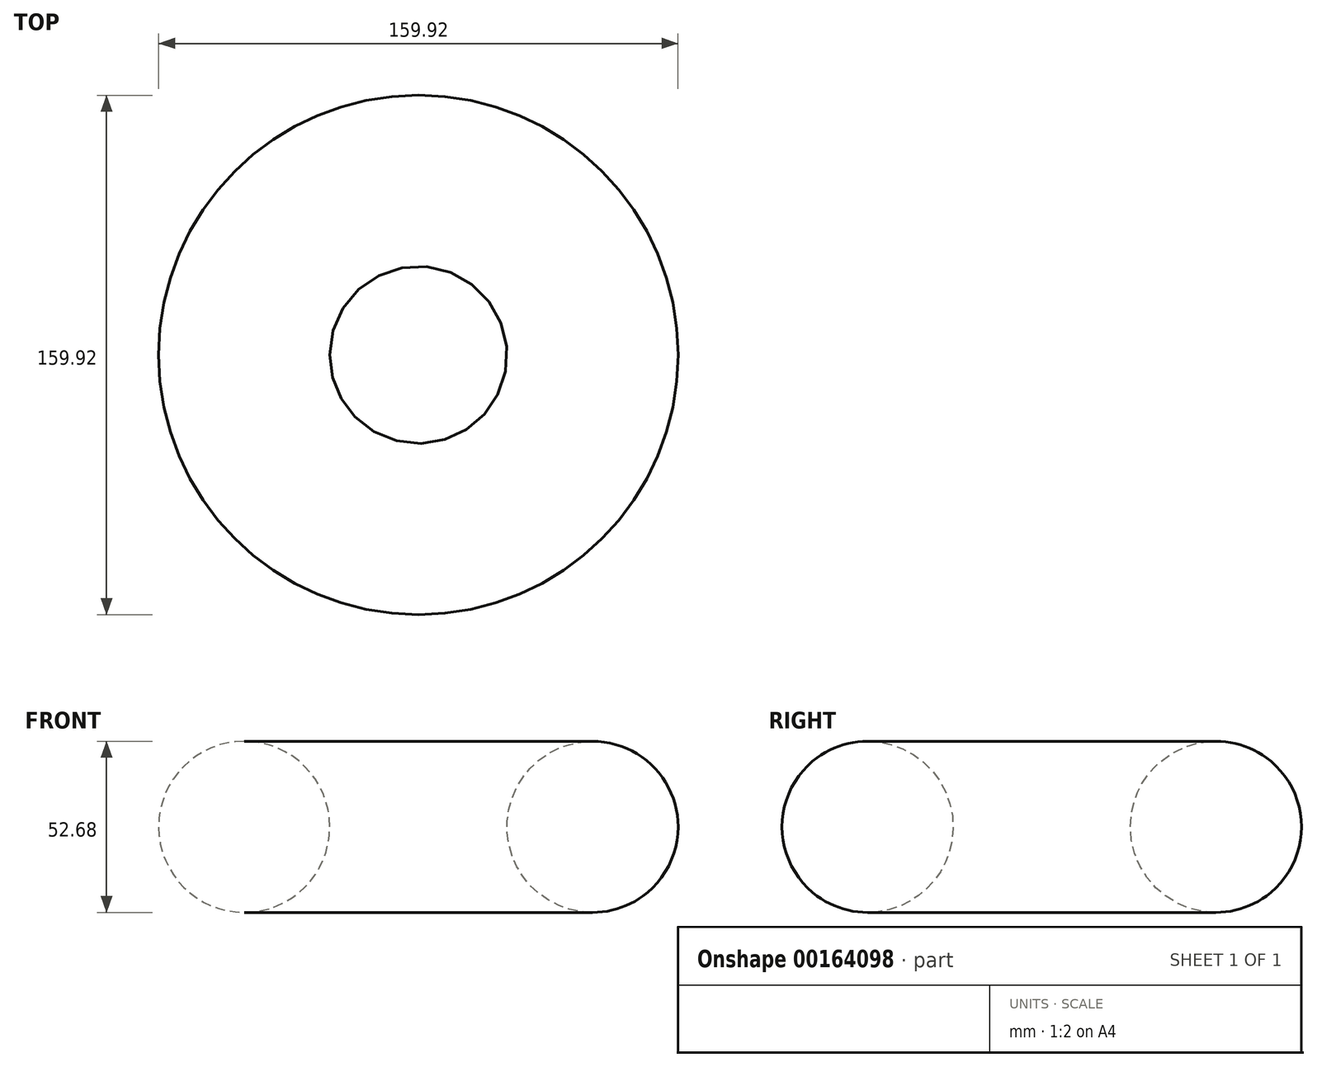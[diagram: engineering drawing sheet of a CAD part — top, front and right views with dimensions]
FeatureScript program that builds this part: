
annotation { "Feature Type Name" : "Feature", "Feature Type Description" : "" }
export const myFeature = defineFeature(function(context is Context, id is Id, definition is map)
    precondition{}
    {
        {
            var Q0;
            Q0=qCreatedBy(makeId("Front.planeOp"),FACE);
            var sketch = newSketch(context, id + "F0", { "sketchPlane" : qUnion([Q0])});
            skCircle(sketch, "E0", {"center": v(-53.62, 22.6) * mm, "radius": 26.34 * mm});
            skLineSegment(sketch, "E1", {"start": v(0, 0) * mm, "end": v(0, 37.76) * mm, "construction": true});
            skSolve(sketch);
        }
        {
            var Q0;
            Q0 = qSketchRegion(id + "F0", true);
            var Q1;
            Q1=sQuery(id+"F0.wireOp",EDGE,"E1");
            revolve(context, id + "F1", {"entities" : qUnion([Q0]), "axis" : qUnion([Q1]), "revolveType" : RevolveType.FULL});
        }
    });
